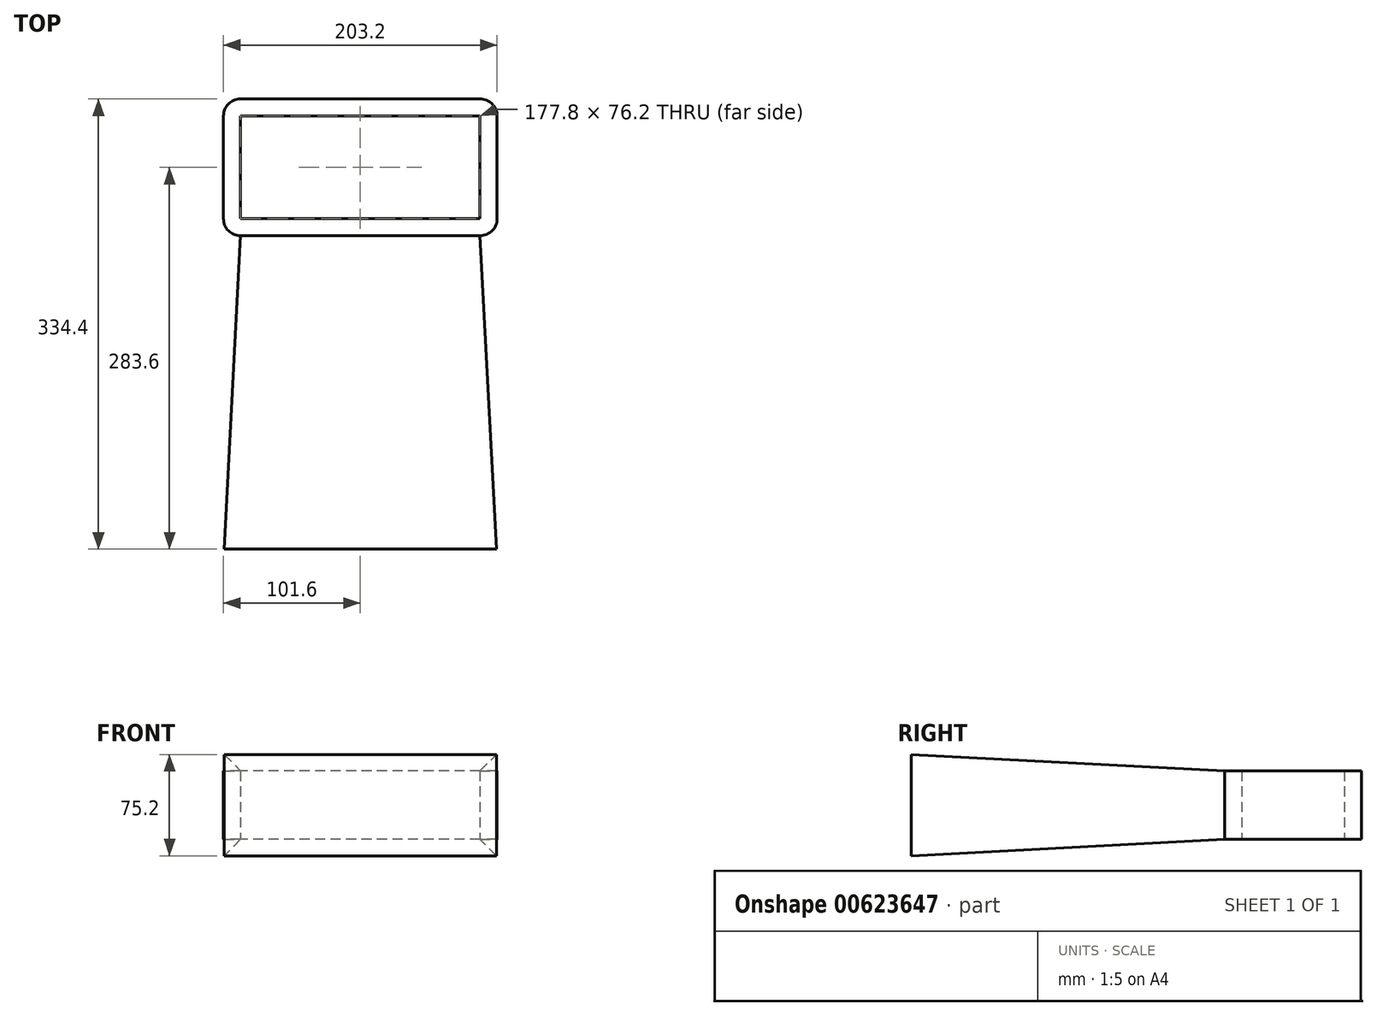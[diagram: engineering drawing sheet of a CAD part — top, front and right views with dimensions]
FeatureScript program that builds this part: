
annotation { "Feature Type Name" : "Feature", "Feature Type Description" : "" }
export const myFeature = defineFeature(function(context is Context, id is Id, definition is map)
    precondition{}
    {
        {
            var Q0;
            Q0=qCreatedBy(makeId("Top.planeOp"),FACE);
            var sketch = newSketch(context, id + "F0", { "sketchPlane" : qUnion([Q0])});
            skLineSegment(sketch, "E0.bottom", {"start": v(88.9, -38.1) * mm, "end": v(-88.9, -38.1) * mm});
            skLineSegment(sketch, "E0.top", {"start": v(88.9, 38.1) * mm, "end": v(-88.9, 38.1) * mm});
            skLineSegment(sketch, "E0.left", {"start": v(88.9, -38.1) * mm, "end": v(88.9, 38.1) * mm});
            skLineSegment(sketch, "E0.right", {"start": v(-88.9, -38.1) * mm, "end": v(-88.9, 38.1) * mm});
            skPoint(sketch, "E0.middle", {"position": v(0, 0) * mm});
            skLineSegment(sketch, "E1.0", {"start": v(88.9, 50.8) * mm, "end": v(-88.9, 50.8) * mm});
            skLineSegment(sketch, "E1.1", {"start": v(101.6, -38.1) * mm, "end": v(101.6, 38.1) * mm});
            skLineSegment(sketch, "E1.2", {"start": v(88.9, -50.8) * mm, "end": v(-88.9, -50.8) * mm});
            skLineSegment(sketch, "E1.3", {"start": v(-101.6, -38.1) * mm, "end": v(-101.6, 38.1) * mm});
            skPoint(sketch, "E2.visualSharp", {"position": v(-101.6, 50.8) * mm});
            skArc(sketch, "E2.filletArc", {"start": v(-88.9, 50.8) * mm, "mid": v(-97.88, 47.08) * mm, "end": v(-101.6, 38.1) * mm});
            skPoint(sketch, "E3.visualSharp", {"position": v(-101.6, -50.8) * mm});
            skArc(sketch, "E3.filletArc", {"start": v(-101.6, -38.1) * mm, "mid": v(-97.88, -47.08) * mm, "end": v(-88.9, -50.8) * mm});
            skPoint(sketch, "E4.visualSharp", {"position": v(101.6, 50.8) * mm});
            skArc(sketch, "E4.filletArc", {"start": v(101.6, 38.1) * mm, "mid": v(97.88, 47.08) * mm, "end": v(88.9, 50.8) * mm});
            skPoint(sketch, "E5.visualSharp", {"position": v(101.6, -50.8) * mm});
            skArc(sketch, "E5.filletArc", {"start": v(88.9, -50.8) * mm, "mid": v(97.88, -47.08) * mm, "end": v(101.6, -38.1) * mm});
            skSolve(sketch);
        }
        {
            var Q0;
            Q0=makeQuery(id+"F0.imprint","IMPRINT",FACE,{"disambiguationData":[TD([[makeQuery(id+"F0.imprint","IMPRINT",EDGE,{"derivedFrom":sQuery(id+"F0.wireOp",EDGE,"E0.bottom")}),1.0]])]});
            extrude(context, id + "F1", {"entities" : qUnion([Q0]), "depth" : 50.8 * mm, "offsetDistance" : 25.4 * mm});
        }
        {
            var Q0;
            Q0=makeQuery(id+"F1.opExtrude","SWEPT_FACE",FACE,{"disambiguationData":[OSD([sQuery(id+"F0.wireOp",EDGE,"E1.2")])]});
            var sketch = newSketch(context, id + "F2", { "sketchPlane" : qUnion([Q0])});
            skSolve(sketch);
        }
        {
            var Q0;
            {var subQ0=sQuery(id+"F0.wireOp",EDGE,"E1.2");Q0=makeQuery(id+"F2.imprint","IMPRINT",FACE,{"disambiguationData":[TD([[makeQuery(id+"F2.imprint","IMPRINT",EDGE,{"derivedFrom":makeQuery(id+"F1.opExtrude","CAP_EDGE",EDGE,{"disambiguationData":[OSD([subQ0])],"isStart":true})}),-1.0]])]});}
            extrude(context, id + "F3", {"entities" : qUnion([Q0]), "operationType" : NewBodyOperationType.ADD, "endBound" : BoundingType.THROUGH_ALL, "depth" : 96.22 * mm, "offsetDistance" : 25.4 * mm, "hasDraft" : true, "draftAngle" : 3 * degree});
        }
    });
